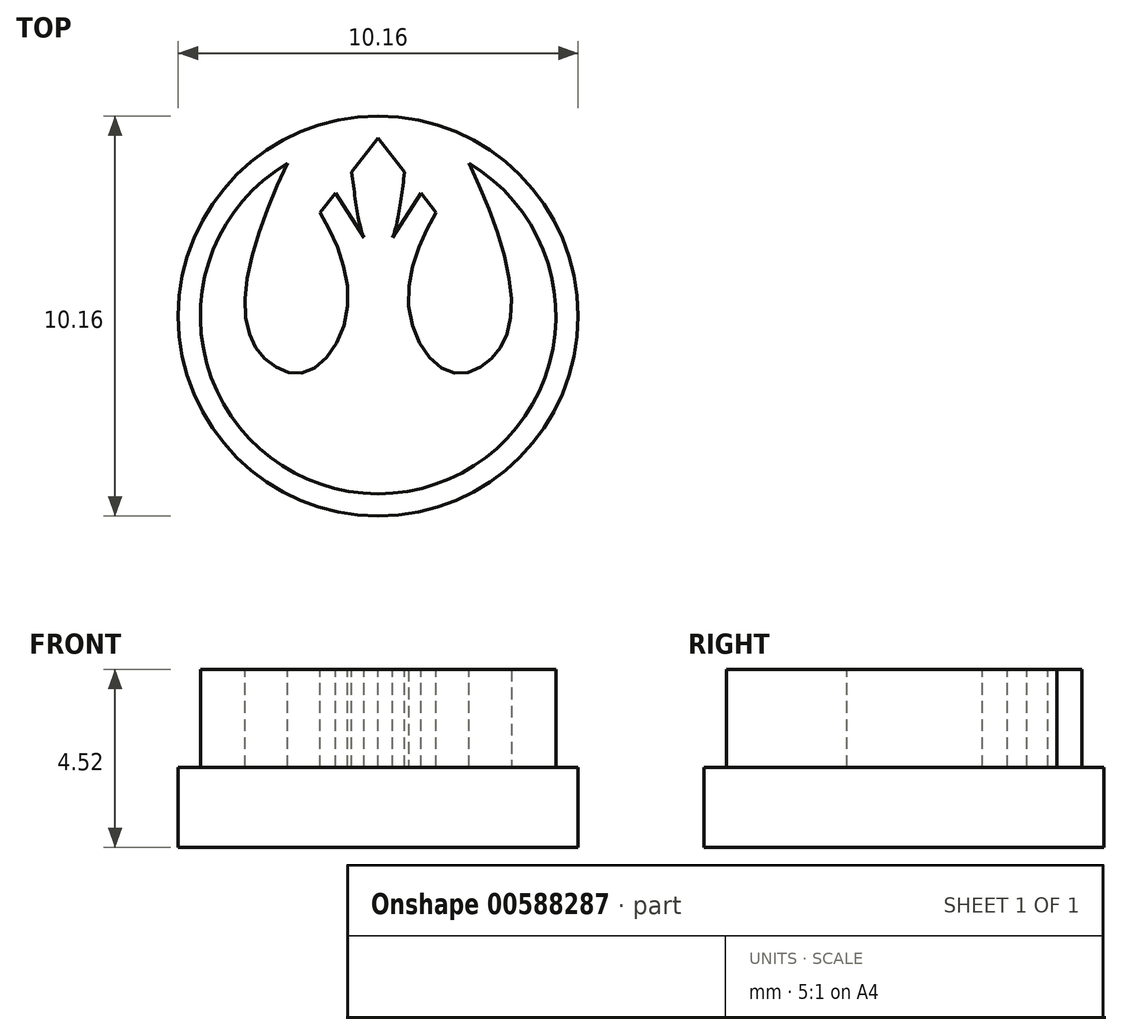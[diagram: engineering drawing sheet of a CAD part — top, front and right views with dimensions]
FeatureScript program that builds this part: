
annotation { "Feature Type Name" : "Feature", "Feature Type Description" : "" }
export const myFeature = defineFeature(function(context is Context, id is Id, definition is map)
    precondition{}
    {
        {
            var Q0;
            Q0=qCreatedBy(makeId("Top.planeOp"),FACE);
            var sketch = newSketch(context, id + "F0", { "sketchPlane" : qUnion([Q0])});
            skLineSegment(sketch, "E0.MirrorCS", {"start": v(8.3, 14.77) * mm, "end": v(6.12, 17.56) * mm});
            skFitSpline(sketch, "E1.MirrorCS", {"points": [v(12.98, 21.83) * mm, v(19.05, 2) * mm, v(15.99, -6.3) * mm, v(9.93, -7.87) * mm, v(4.38, 1.25) * mm, v(8.3, 14.77) * mm], "startDerivative": vector(33.92, -70.48) * mm, "endDerivative": vector(30.58, 50.45) * mm});
            skCircle(sketch, "E2", {"center": v(0, 0) * mm, "radius": 25.4 * mm});
            skLineSegment(sketch, "E3.trimOffspring", {"start": v(3.77, 20.58) * mm, "end": v(0, 25.4) * mm});
            skCircle(sketch, "E4", {"center": v(0, 0) * mm, "radius": 28.58 * mm});
            skLineSegment(sketch, "E5", {"start": v(0, 25.4) * mm, "end": v(3.77, 20.58) * mm});
            skFitSpline(sketch, "E6", {"points": [v(3.77, 20.58) * mm, v(2.04, 11.2) * mm, v(0.6, 9.18) * mm], "startDerivative": vector(-2.05, -16.88) * mm, "endDerivative": vector(-4.57, -4.59) * mm});
            skPoint(sketch, "E7.trimOffspring.end.orphan", {"position": v(0, 25.4) * mm});
            skPoint(sketch, "E8.start.orphan", {"position": v(-12.98, 21.83) * mm});
            skLineSegment(sketch, "E9", {"start": v(6.12, 17.56) * mm, "end": v(2.04, 11.2) * mm});
            skFitSpline(sketch, "E10.MirrorCS", {"points": [v(-12.98, 21.83) * mm, v(-19.05, 2) * mm, v(-15.99, -6.3) * mm, v(-9.93, -7.87) * mm, v(-4.38, 1.25) * mm, v(-8.3, 14.77) * mm], "startDerivative": vector(-33.92, -70.48) * mm, "endDerivative": vector(-30.58, 50.45) * mm});
            skLineSegment(sketch, "E11.MirrorCS", {"start": v(-8.3, 14.77) * mm, "end": v(-6.12, 17.56) * mm});
            skLineSegment(sketch, "E12.MirrorCS", {"start": v(0, 25.4) * mm, "end": v(-3.77, 20.58) * mm});
            skLineSegment(sketch, "E13.MirrorCS", {"start": v(-6.12, 17.56) * mm, "end": v(-2.04, 11.2) * mm});
            skFitSpline(sketch, "E14.MirrorCS", {"points": [v(-3.77, 20.58) * mm, v(-2.04, 11.2) * mm, v(-0.6, 9.18) * mm], "startDerivative": vector(2.05, -16.88) * mm, "endDerivative": vector(4.57, -4.59) * mm});
            skSolve(sketch);
        }
        {
            var Q0;
            Q0=qCreatedBy(makeId("Top.planeOp"),FACE);
            var sketch = newSketch(context, id + "F1", { "sketchPlane" : qUnion([Q0])});
            skCircle(sketch, "E15", {"center": v(0, 0) * mm, "radius": 28.57 * mm});
            skSolve(sketch);
        }
        {
            var Q0;
            Q0 = qSketchRegion(id + "F1", true);
            extrude(context, id + "F2", {"entities" : qUnion([Q0]), "oppositeDirection" : true, "depth" : 25.4 * mm, "offsetDistance" : 25.4 * mm});
        }
        {
            var Q0;
            Q0=makeQuery(id+"F0.imprint","IMPRINT",FACE,{"disambiguationData":[TD([[makeQuery(id+"F0.imprint","IMPRINT",EDGE,{"derivedFrom":sQuery(id+"F0.wireOp",EDGE,"E4")}),1.0]])]});
            var Q1;
            {var subQ1=sQuery(id+"F0.wireOp",EDGE,"E10.MirrorCS");Q1=makeQuery(id+"F0.imprint","IMPRINT",FACE,{"disambiguationData":[TD([[makeQuery(id+"F0.imprint","IMPRINT",EDGE,{"derivedFrom":subQ1}),1.0]])]});}
            var Q2;
            Q2=makeQuery(id+"F0.imprint","IMPRINT",FACE,{"disambiguationData":[TD([[makeQuery(id+"F0.imprint","IMPRINT",EDGE,{"derivedFrom":sQuery(id+"F0.wireOp",EDGE,"E0.MirrorCS")}),-1.0]])]});
            extrude(context, id + "F3", {"entities" : qUnion([Q0, Q1, Q2]), "operationType" : NewBodyOperationType.REMOVE, "oppositeDirection" : true, "depth" : 13.97 * mm, "offsetDistance" : 25.4 * mm});
        }
        {
            var Q0;
            Q0=makeQuery(id+"F2.opExtrude","SWEPT_BODY",BODY,{"disambiguationData":[OSD([sQuery(id+"F1.wireOp",EDGE,"E15")])]});
            var Q1;
            Q1=qCreatedBy(makeId("Origin.pointOp"),VERTEX);
            transform(context, id + "F4", {"entities" : qUnion([Q0]), "transformType" : TransformType.SCALE_UNIFORMLY, "scale" : .1777778, "scalePoint" : qUnion([Q1]), "makeCopy" : false});
        }
    });
